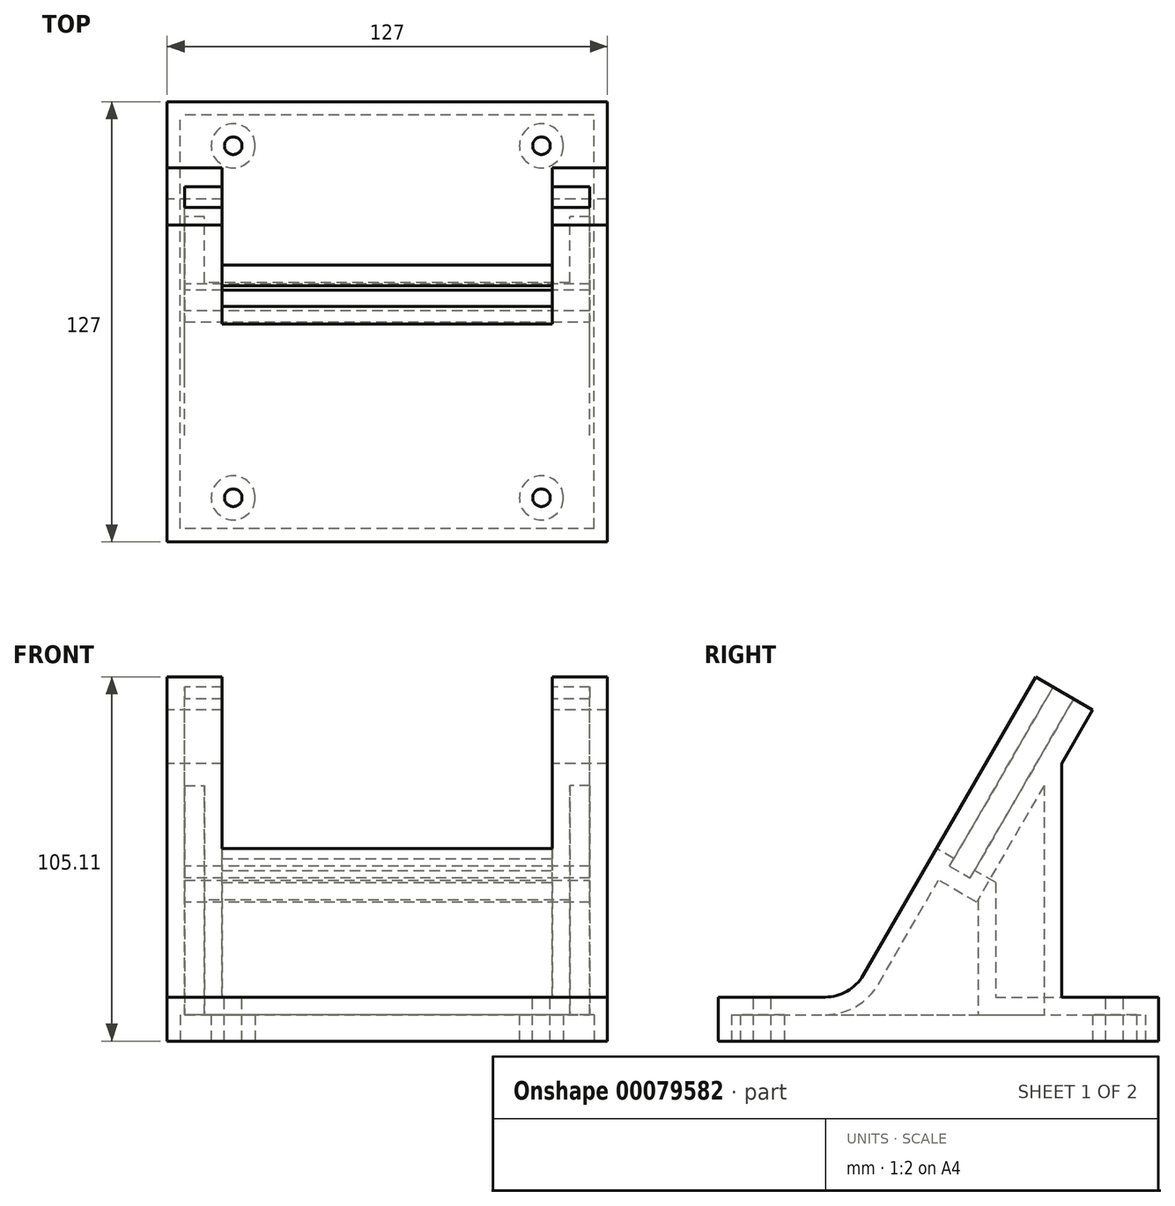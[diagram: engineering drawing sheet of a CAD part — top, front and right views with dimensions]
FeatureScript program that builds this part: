
annotation { "Feature Type Name" : "Feature", "Feature Type Description" : "" }
export const myFeature = defineFeature(function(context is Context, id is Id, definition is map)
    precondition{}
    {
        {
            var Q0;
            Q0=qCreatedBy(makeId("Right.planeOp"),FACE);
            var sketch = newSketch(context, id + "F0", { "sketchPlane" : qUnion([Q0])});
            skLineSegment(sketch, "E0.bottom", {"start": v(0, 0) * mm, "end": v(127, 0) * mm});
            skLineSegment(sketch, "E0.top", {"start": v(0, 12.7) * mm, "end": v(30.77, 12.7) * mm});
            skLineSegment(sketch, "E0.left", {"start": v(0, 0) * mm, "end": v(0, 12.7) * mm});
            skLineSegment(sketch, "E0.right", {"start": v(127, 0) * mm, "end": v(127, 12.7) * mm});
            skLineSegment(sketch, "E1", {"start": v(41.77, 19.05) * mm, "end": v(88.9, 100.69) * mm});
            skLineSegment(sketch, "E2.0", {"start": v(98.97, 80.03) * mm, "end": v(107.95, 95.58) * mm});
            skLineSegment(sketch, "E3.trimOffspring", {"start": v(98.97, 12.7) * mm, "end": v(127, 12.7) * mm});
            skPoint(sketch, "E4.visualSharp", {"position": v(38.1, 12.7) * mm});
            skArc(sketch, "E4.filletArc", {"start": v(30.77, 12.7) * mm, "mid": v(37.12, 14.4) * mm, "end": v(41.77, 19.05) * mm});
            skPoint(sketch, "E5.visualSharp", {"position": v(60.1, 12.7) * mm});
            skLineSegment(sketch, "E6", {"start": v(88.9, 100.69) * mm, "end": v(91.45, 105.1) * mm});
            skLineSegment(sketch, "E7", {"start": v(107.95, 95.58) * mm, "end": v(91.45, 105.1) * mm});
            skLineSegment(sketch, "E8", {"start": v(98.97, 80.03) * mm, "end": v(98.97, 12.7) * mm});
            skSolve(sketch);
        }
        {
            var Q0;
            Q0=makeQuery(id+"F0.imprint","IMPRINT",FACE,{"disambiguationData":[TD([[makeQuery(id+"F0.imprint","IMPRINT",EDGE,{"derivedFrom":sQuery(id+"F0.wireOp",EDGE,"E0.bottom")}),1.0]])]});
            extrude(context, id + "F1", {"entities" : qUnion([Q0]), "depth" : 127 * mm});
        }
        {
            var Q0;
            Q0=makeQuery(id+"F1.opExtrude","SWEPT_FACE",FACE,{"disambiguationData":[OSD([sQuery(id+"F0.wireOp",EDGE,"E1")])]});
            var sketch = newSketch(context, id + "F2", { "sketchPlane" : qUnion([Q0])});
            skLineSegment(sketch, "E9.bottom", {"start": v(111.13, 136.75) * mm, "end": v(15.88, 136.75) * mm});
            skLineSegment(sketch, "E9.top", {"start": v(15.88, 79.6) * mm, "end": v(111.13, 79.6) * mm});
            skLineSegment(sketch, "E9.left", {"start": v(111.13, 136.75) * mm, "end": v(111.13, 79.6) * mm});
            skLineSegment(sketch, "E9.right", {"start": v(15.87, 136.75) * mm, "end": v(15.88, 79.6) * mm});
            skSolve(sketch);
        }
        {
            var Q0;
            Q0=makeQuery(id+"F2.imprint","IMPRINT",FACE,{"disambiguationData":[TD([[makeQuery(id+"F2.imprint","IMPRINT",EDGE,{"derivedFrom":sQuery(id+"F2.wireOp",EDGE,"E9.bottom")}),1.0]])]});
            extrude(context, id + "F3", {"entities" : qUnion([Q0]), "operationType" : NewBodyOperationType.REMOVE, "endBound" : BoundingType.THROUGH_ALL, "oppositeDirection" : true, "depth" : 25.4 * mm});
        }
        {
            var Q0;
            Q0=makeQuery(id+"F1.opExtrude","SWEPT_FACE",FACE,{"disambiguationData":[OSD([sQuery(id+"F0.wireOp",EDGE,"E0.top")])]});
            var sketch = newSketch(context, id + "F4", { "sketchPlane" : qUnion([Q0])});
            skCircle(sketch, "E10", {"center": v(19.05, 12.7) * mm, "radius": 2.54 * mm});
            skCircle(sketch, "E11", {"center": v(107.95, 12.7) * mm, "radius": 2.54 * mm});
            skSolve(sketch);
        }
        {
            var Q0;
            Q0=makeQuery(id+"F4.imprint","IMPRINT",FACE,{"disambiguationData":[TD([[makeQuery(id+"F4.imprint","IMPRINT",EDGE,{"derivedFrom":sQuery(id+"F4.wireOp",EDGE,"E10")}),1.0]])]});
            var Q1;
            Q1=makeQuery(id+"F4.imprint","IMPRINT",FACE,{"disambiguationData":[TD([[makeQuery(id+"F4.imprint","IMPRINT",EDGE,{"derivedFrom":sQuery(id+"F4.wireOp",EDGE,"E11")}),1.0]])]});
            extrude(context, id + "F5", {"entities" : qUnion([Q0, Q1]), "operationType" : NewBodyOperationType.REMOVE, "endBound" : BoundingType.THROUGH_ALL, "oppositeDirection" : true, "depth" : 25.4 * mm});
        }
        {
            var Q0;
            Q0=makeQuery(id+"F1.opExtrude","SWEPT_FACE",FACE,{"disambiguationData":[OSD([sQuery(id+"F0.wireOp",EDGE,"E3.trimOffspring")])]});
            var sketch = newSketch(context, id + "F6", { "sketchPlane" : qUnion([Q0])});
            skCircle(sketch, "E12", {"center": v(19.05, 114.3) * mm, "radius": 2.54 * mm});
            skCircle(sketch, "E13", {"center": v(107.95, 114.3) * mm, "radius": 2.54 * mm});
            skSolve(sketch);
        }
        {
            var Q0;
            Q0=makeQuery(id+"F6.imprint","IMPRINT",FACE,{"disambiguationData":[TD([[makeQuery(id+"F6.imprint","IMPRINT",EDGE,{"derivedFrom":sQuery(id+"F6.wireOp",EDGE,"E12")}),1.0]])]});
            var Q1;
            Q1=makeQuery(id+"F6.imprint","IMPRINT",FACE,{"disambiguationData":[TD([[makeQuery(id+"F6.imprint","IMPRINT",EDGE,{"derivedFrom":sQuery(id+"F6.wireOp",EDGE,"E13")}),1.0]])]});
            extrude(context, id + "F7", {"entities" : qUnion([Q0, Q1]), "operationType" : NewBodyOperationType.REMOVE, "endBound" : BoundingType.THROUGH_ALL, "oppositeDirection" : true, "depth" : 25.4 * mm});
        }
        {
            var Q0;
            {var subQ0=sQuery(id+"F0.wireOp",EDGE,"E7");Q0=makeQuery(id+"F3.boolean.opBoolean","SPLIT",FACE,{"disambiguationData":[TD([makeQuery(id+"F3.opExtrude","SWEPT_FACE",FACE,{"disambiguationData":[OSD([sQuery(id+"F2.wireOp",EDGE,"E9.left")])]})])],"derivedFrom":makeQuery(id+"F1.opExtrude","SWEPT_FACE",FACE,{"disambiguationData":[OSD([subQ0])]})});}
            var sketch = newSketch(context, id + "F8", { "sketchPlane" : qUnion([Q0])});
            skLineSegment(sketch, "E14.bottom", {"start": v(121.92, 32.49) * mm, "end": v(5.08, 32.49) * mm});
            skLineSegment(sketch, "E14.top", {"start": v(121.92, 39.35) * mm, "end": v(5.08, 39.35) * mm});
            skLineSegment(sketch, "E14.left", {"start": v(121.92, 32.49) * mm, "end": v(121.92, 39.35) * mm});
            skLineSegment(sketch, "E14.right", {"start": v(5.08, 32.49) * mm, "end": v(5.08, 39.35) * mm});
            skSolve(sketch);
        }
        {
            var Q0;
            {var subQ0=sQuery(id+"F8.wireOp",EDGE,"E14.right");Q0=makeQuery(id+"F8.imprint","IMPRINT",FACE,{"disambiguationData":[TD([[makeQuery(id+"F8.imprint","IMPRINT",EDGE,{"derivedFrom":subQ0}),-1.0]])]});}
            var Q1;
            {var subQ0=sQuery(id+"F8.wireOp",EDGE,"E14.left");Q1=makeQuery(id+"F8.imprint","IMPRINT",FACE,{"disambiguationData":[TD([[makeQuery(id+"F8.imprint","IMPRINT",EDGE,{"derivedFrom":subQ0}),1.0]])]});}
            extrude(context, id + "F9", {"entities" : qUnion([Q0, Q1]), "operationType" : NewBodyOperationType.REMOVE, "oppositeDirection" : true, "depth" : 59.69 * mm});
        }
        {
            var Q0;
            Q0=makeQuery(id+"F1.opExtrude","SWEPT_FACE",FACE,{"disambiguationData":[OSD([sQuery(id+"F0.wireOp",EDGE,"E8")])]});
            var sketch = newSketch(context, id + "F10", { "sketchPlane" : qUnion([Q0])});
            skLineSegment(sketch, "E15.bottom", {"start": v(-111.13, 53.61) * mm, "end": v(-15.88, 53.61) * mm});
            skLineSegment(sketch, "E15.top", {"start": v(-111.13, 12.7) * mm, "end": v(-15.88, 12.7) * mm});
            skLineSegment(sketch, "E15.left", {"start": v(-111.13, 53.61) * mm, "end": v(-111.13, 12.7) * mm});
            skLineSegment(sketch, "E15.right", {"start": v(-15.88, 53.61) * mm, "end": v(-15.88, 12.7) * mm});
            skSolve(sketch);
        }
        {
            var Q0;
            {var subQ0=sQuery(id+"F10.wireOp",EDGE,"E15.top");Q0=makeQuery(id+"F10.imprint","IMPRINT",FACE,{"disambiguationData":[TD([[makeQuery(id+"F10.imprint","IMPRINT",EDGE,{"derivedFrom":subQ0}),1.0]])]});}
            var Q1;
            {var subQ0=sQuery(id+"F10.wireOp",EDGE,"E15.bottom");Q1=makeQuery(id+"F10.imprint","IMPRINT",FACE,{"disambiguationData":[TD([[makeQuery(id+"F10.imprint","IMPRINT",EDGE,{"derivedFrom":subQ0}),-1.0]])]});}
            extrude(context, id + "F11", {"entities" : qUnion([Q0, Q1]), "operationType" : NewBodyOperationType.REMOVE, "oppositeDirection" : true, "depth" : 19.05 * mm});
        }
        {
            var Q0;
            Q0=makeQuery(id+"F1.opExtrude","SWEPT_FACE",FACE,{"disambiguationData":[OSD([sQuery(id+"F0.wireOp",EDGE,"E0.bottom")])]});
            var sketch = newSketch(context, id + "F12", { "sketchPlane" : qUnion([Q0])});
            skLineSegment(sketch, "E16.0", {"start": v(3.81, -3.81) * mm, "end": v(3.81, -123.2) * mm});
            skLineSegment(sketch, "E16.1", {"start": v(123.2, -3.81) * mm, "end": v(3.8, -3.81) * mm});
            skLineSegment(sketch, "E16.2", {"start": v(123.2, -3.81) * mm, "end": v(123.2, -123.2) * mm});
            skLineSegment(sketch, "E16.3", {"start": v(123.2, -123.2) * mm, "end": v(3.8, -123.2) * mm});
            skCircle(sketch, "E17.0", {"center": v(107.95, -12.7) * mm, "radius": 6.35 * mm});
            skCircle(sketch, "E18.0", {"center": v(19.05, -12.7) * mm, "radius": 6.35 * mm});
            skCircle(sketch, "E19.0", {"center": v(19.05, -114.3) * mm, "radius": 6.35 * mm});
            skCircle(sketch, "E20.0", {"center": v(107.95, -114.3) * mm, "radius": 6.35 * mm});
            skSolve(sketch);
        }
        {
            var Q0;
            Q0=makeQuery(id+"F12.imprint","IMPRINT",FACE,{"disambiguationData":[TD([[makeQuery(id+"F12.imprint","IMPRINT",EDGE,{"derivedFrom":sQuery(id+"F12.wireOp",EDGE,"E16.0")}),1.0]])]});
            extrude(context, id + "F13", {"entities" : qUnion([Q0]), "operationType" : NewBodyOperationType.REMOVE, "oppositeDirection" : true, "depth" : 7.62 * mm});
        }
        {
            var Q0;
            Q0=makeQuery(id+"F13.boolean.opBoolean","COPY",FACE,{"derivedFrom":makeQuery(id+"F13.opExtrude","CAP_FACE",FACE,{"disambiguationData":[OSD([sQuery(id+"F12.wireOp",EDGE,"E16.0"),sQuery(id+"F12.wireOp",EDGE,"E16.1"),sQuery(id+"F12.wireOp",EDGE,"E16.2"),sQuery(id+"F12.wireOp",EDGE,"E16.3"),sQuery(id+"F12.wireOp",EDGE,"E17.0"),sQuery(id+"F12.wireOp",EDGE,"E18.0"),sQuery(id+"F12.wireOp",EDGE,"E19.0"),sQuery(id+"F12.wireOp",EDGE,"E20.0")])],"isStart":false})});
            shell(context, id + "F14", {"entities" : qUnion([Q0]), "thickness" : 5.08 * mm});
        }
    });
